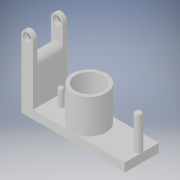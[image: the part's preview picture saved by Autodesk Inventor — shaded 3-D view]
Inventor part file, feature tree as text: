
AUTODESK INVENTOR PART (.ipt)
format: ipt  version: 2019 (Build 230136000, 136)  size: 182,272 bytes
history: native  units: in
note: dims shown in document units (in); Inventor stores cm internally (conversion verified against a paired STEP export)
features: sketch x6, extrude x5, fillet x3
ambient origin geometry x8: Origin, YZ Plane, XZ Plane, XY Plane, X Axis, Y Axis, Z Axis, Center Point
bodies: Solid1 (feature_tree)
feature tree (14):
  extrude  "Extrusion1"  Depth=0.1969in
  extrude  "Extrusion2"  Depth=0.1969in
  extrude  "Extrusion3"  Depth=2.126in
  fillet  "Fillet1"  Radius=0.7874in
  fillet  "Fillet2"  Radius=0.1181in
  extrude  "Extrusion4"  Depth=0.7874in
  sketch  "Sketch6"  dims[d13=0.2559in d14=0.7874in]
  extrude  "Extrusion5"  Depth=0.3937in
  sketch  "Sketch8"  dims[d21=0.3937in d22=0.6693in d23=0.7874in d24=0.0in d25=0.3937in d26=0.7874in d27=0.0in d28=0.0394in d29=0.0394in d30=0.6299in d31=1.1811in d32=0.0in d40=0.5512in d41=0.5512in d42=0.5906in d43=0.5512in d44=0.0in d46=2.4016in d47=1.2205in d48=2.3228in d49=1.1811in d50=0.5315in d51=0.1378in]
  fillet  "Fillet4"  Radius=0.1575in
  sketch  "Sketch1"  dims[d0=1.5748in d2=0.1969in]
  sketch  "Sketch4"  dims[d6=0.1378in d7=0.1969in]
  sketch  "Sketch5"  dims[d8=0.2756in d9=2.126in d10=0.7874in d11=0.0in d12=0.1181in]
  sketch  "Sketch7"  dims[d16=0.9055in d19=0.3937in d20=0.1575in]
